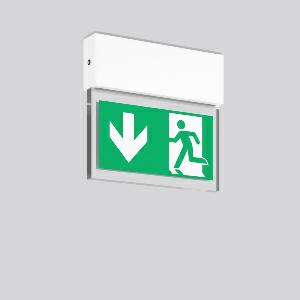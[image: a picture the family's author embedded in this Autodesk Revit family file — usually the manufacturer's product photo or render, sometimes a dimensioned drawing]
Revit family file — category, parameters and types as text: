
# Revit family: halyxx_671736_002_1_89_842c
name_source: partatom
category: Lighting Fixtures
units: mm (PartAtom-declared; Revit-internal decimal feet)

## family parameters
Cut with Voids When Loaded = No
Host = Face
Light Source = No
Part Type = Normal
Room Calculation Point = No
Round Connector Dimension = Use Diameter
Shared = No

## types (1)
- HALYXX (1 x LED Modul 840, 60 lm, 4000)
    Apparent Load = 3 VA
    Approval mark = CE
    CIE Flux Codes = 18 46 76 54 100
    Color Rendering = 80
    Color Temperature = 4000
    Default Elevation = 1800 mm
    Description = Series: HALYXX
Luminaire for escape route identification. Housing: extruded aluminium profile, anodised or powder-coated. Display panel: highly transparent panel, plastic, with legend on one side/both sides. Driver integrated. Suitable for connection to central battery systems. With AC Control monitoring module for LUXIFAIR central battery units. Please indicate legend number when placing your order! 
Colour: white
Length: 235 mm
Width: 40 mm
Height: 220 mm
Weight: 1.35 kg
Operating mode: maintained power mode
Viewing Distance: 19 m
Lamp: LED
Socket: without socket
Colour temperature: 4000K
Colour rendering index (CRI): 80
System power: 3 W
Rated luminous flux: 60 lm
Luminous flux, emergency: 60
System power, emergency: 2.8 W
Control gear: Regulated power supply
Protection class: I
Type of protection: IP 40
    Height = 220 mm
    Lamp = 1 x LED Modul 840
    Lamp Light Flux = 60 lm
    Lamp count = 1
    Length = 235 mm
    Lifetime = 50000 h
    Luminous efficacy = 20 lm/W
    Manufacturer = RZB
    ModVariant = No
    Model = 671736.002.1.89
    Mounting Place = Ceiling
    Mounting Type = Surface mounted
    Number of Poles = 1
    OnlyDefault = Yes
    Power Factor = 1
    Product Name = HALYXX
    Product group = Surface mounted ceiling luminaires
    ProductGroupID = 303
    Protection Class = Protection class I
    Protection Degree = IP 40
    RLX_Detail_Level = 1
    RLX_Emergency_Light_Flux = 60 lm
    RLX_Emergency_Type = 3
    RLX_Emergency_Type_DB = Yes
    RlxData = <blob elided: 40845 chars, md5=61986006>
    Socket = socket
    Standby Power = 0 W
    System Light Flux = 60 lm
    System Power = 3 W
    Type Comments = Product without accessories
    Type Image = 671742.002.jpg
    URL = http://relux.com
    VarID = ---
    Voltage = 230 V
    Voltage Range = 220-240 V
    Weight = 0.00 kg
    Width = 40 mm

## geometry (parser evidence)
native form markers: Blend x4, Sweep x12
no freeform markers — native parametric forms only
